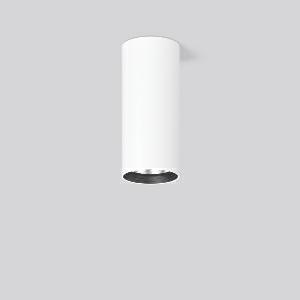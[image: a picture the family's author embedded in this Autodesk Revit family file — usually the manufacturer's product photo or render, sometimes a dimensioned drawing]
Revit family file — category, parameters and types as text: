
# Revit family: heledon_mini_a_931209_002_d5f2
name_source: partatom
category: Lighting Fixtures
units: mm (PartAtom-declared; Revit-internal decimal feet)

## family parameters
Cut with Voids When Loaded = No
Host = Face
Light Source = No
Part Type = Normal
Room Calculation Point = No
Round Connector Dimension = Use Diameter
Shared = No

## types (1)
- HELEDON mini A (1 x LED Modul 930, 3500 lm, 3000)
    Apparent Load = 29 VA
    Approval mark = CE
    CIE Flux Codes = 99 100 100 100 100
    Color Rendering = 90
    Color Temperature = 3000
    Default Elevation = 1800 mm
    Description = Series: HELEDON mini
Cylindrical surface-mounted downlight. Housing: die-cast aluminium, powder-coated. Internal ceiling frame polycarbonate with bayonet mounting. Black plastic ring and recessed LED to prevent glare from the side. Optical assembly with reflector made of MIRO-Silver with 98% total light reflection for outstanding efficiency - can be changed without tools. Best colour rendering index Ra>90. Suitable for Ceiling mounting. Easy installation with a separate ceiling frame with bayonet mounting and plug connection. Driver integrated. Connected via plug-in connector. High quality converter without flickering and stroboscopic effect. The following accessories can be mounted without use of tools: interchangeable lenses, decorative glasses, honeycomb louvre, clear and frosted diffusers, white interchangeable plastic ring. 
Colour: traffic white, matt (RAL 9016)
Diameter: 87 mm
Height: 197 mm
Lamp: LED
Socket: without socket
Colour temperature: 3000K
Colour rendering index (CRI): 92
System power: 29 W
Rated luminous flux: 3500 lm
Luminous efficiency: 121 lm/W
Control gear: Regulated power supply
Protection class: I
Type of protection: IP 20
    Height = 197 mm
    Lamp = 1 x LED Modul 930
    Lamp Light Flux = 3500 lm
    Lamp count = 1
    Length = 87 mm
    Lifetime = 50000 h
    Luminous efficacy = 121 lm/W
    Manufacturer = RZB
    ModVariant = No
    Model = 931209.002
    Mounting Place = Ceiling
    Mounting Type = Surface mounted
    Number of Poles = 1
    OnlyDefault = Yes
    Power Factor = 1
    Product Name = HELEDON mini A
    Product group = Surface mounted downlights
    ProductGroupID = 302
    Protection Class = Protection class I
    Protection Degree = IP 20
    RLX_Detail_Level = 1
    RLX_Emergency_Light_Flux = 0 lm
    RLX_Emergency_Type = 0
    RLX_Emergency_Type_DB = No
    RlxData = <blob elided: 105473 chars, md5=e4472a4f>
    Socket = socket
    Standby Power = 0 W
    System Light Flux = 3500 lm
    System Power = 29 W
    Type Comments = Product without accessories
    Type Image = 931188.002.jpg
    URL = http://relux.com
    VarID = ---
    Voltage = 230 V
    Voltage Range = 220-240 V
    Weight = 0.00 kg
    Width = 0 mm  [stored 0 ft]

note: [stored X ft] marks values corroborated as IEEE doubles in the binary element streams (Revit-internal decimal feet)

## geometry (parser evidence)
native form markers: Blend x4, Sweep x9
no freeform markers — native parametric forms only
